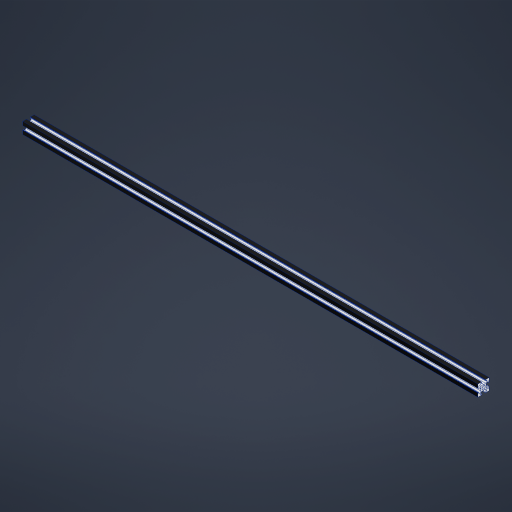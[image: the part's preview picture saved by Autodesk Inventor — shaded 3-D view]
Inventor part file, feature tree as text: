
AUTODESK INVENTOR PART (.ipt)
format: ipt  version: 2024.2 (Build 282272000, 272)  size: 318,464 bytes
history: native  units: mm
features: extrude x1, sketch x1
ambient origin geometry x8: Origin, YZ Plane, XZ Plane, XY Plane, X Axis, Y Axis, Z Axis, Center Point
bodies: Solid1 (feature_tree)
feature tree (2):
  extrude  "Extrusion1"  Depth=0.5mm
  sketch  "Sketch1"  dims[d2=6.5mm d3=0.5mm d4=4.0mm d5=3.465mm d6=5.48mm d7=0.795mm d8=0.305mm d9=2.95mm d11=0.75mm d14=45.0deg d15=10.0mm d16=1.0mm d17=3.0mm d18=45.0deg d19=40.0mm d21=360.0deg d23=800.0mm d24=0.0mm]
